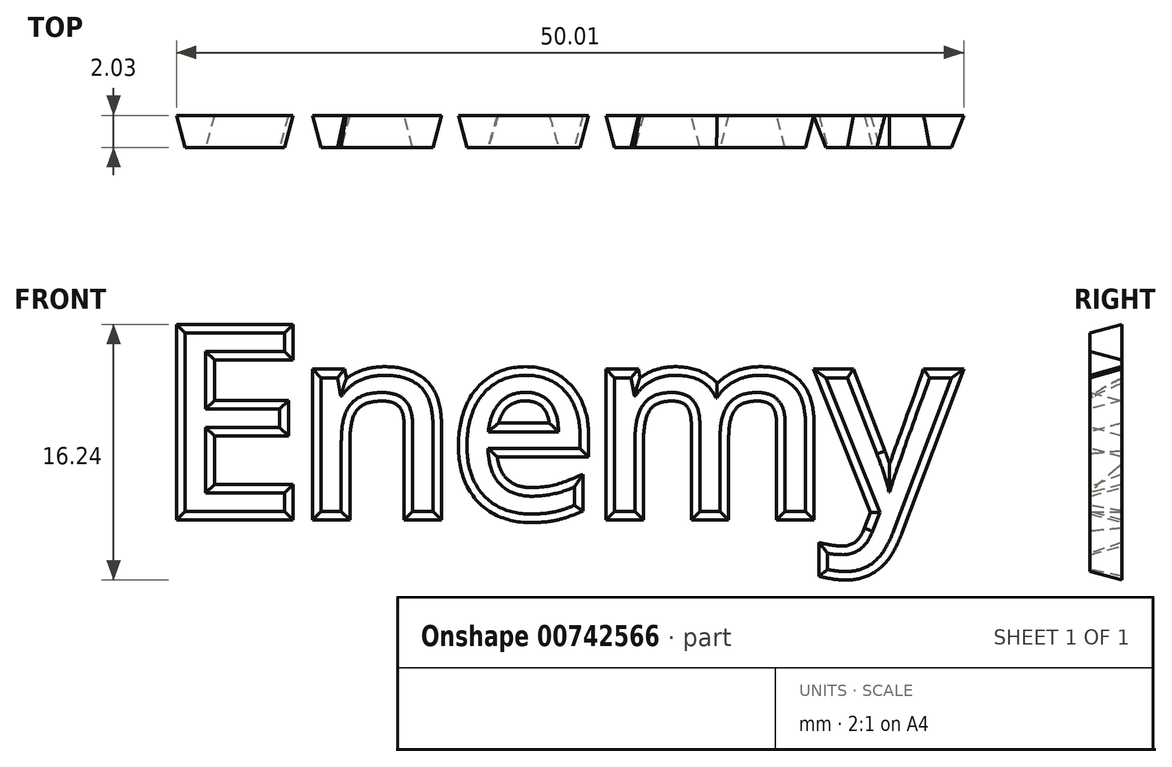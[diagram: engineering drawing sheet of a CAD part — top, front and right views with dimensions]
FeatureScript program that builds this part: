
annotation { "Feature Type Name" : "Feature", "Feature Type Description" : "" }
export const myFeature = defineFeature(function(context is Context, id is Id, definition is map)
    precondition{}
    {
        {
            var Q0;
            Q0=qCreatedBy(makeId("Front.planeOp"),FACE);
            var sketch = newSketch(context, id + "F0", { "sketchPlane" : qUnion([Q0])});
            skLineSegment(sketch, "E0.bottom", {"start": v(-25.4, 15.88) * mm, "end": v(25.4, 15.88) * mm});
            skLineSegment(sketch, "E0.top", {"start": v(-25.4, -15.88) * mm, "end": v(25.4, -15.88) * mm});
            skLineSegment(sketch, "E0.left", {"start": v(-25.4, 15.88) * mm, "end": v(-25.4, -15.88) * mm});
            skLineSegment(sketch, "E0.right", {"start": v(25.4, 15.87) * mm, "end": v(25.4, -15.88) * mm});
            skPoint(sketch, "E0.middle", {"position": v(0, 0) * mm});
            skSolve(sketch);
        }
        {
            var Q0;
            Q0=qCreatedBy(makeId("Front.planeOp"),FACE);
            var sketch = newSketch(context, id + "F1", { "sketchPlane" : qUnion([Q0])});
            skText(sketch, "E1", { "text": "Enemy", "fontName": "OpenSans-Regular.ttf"});
            const initialGuessF1  = {"E1": [-0.02563, -0.00572, 1, 0, 0.01143]};
            skSetInitialGuess(sketch, initialGuessF1);
            skSolve(sketch);
        }
        {
            var Q0;
            Q0=qSketchRegion(id+"F1",true);
            extrude(context, id + "F2", {"entities" : qUnion([Q0]), "oppositeDirection" : true, "depth" : 2.03 * mm, "offsetDistance" : 25.4 * mm, "hasDraft" : true, "draftAngle" : 15 * degree});
        }
    });
